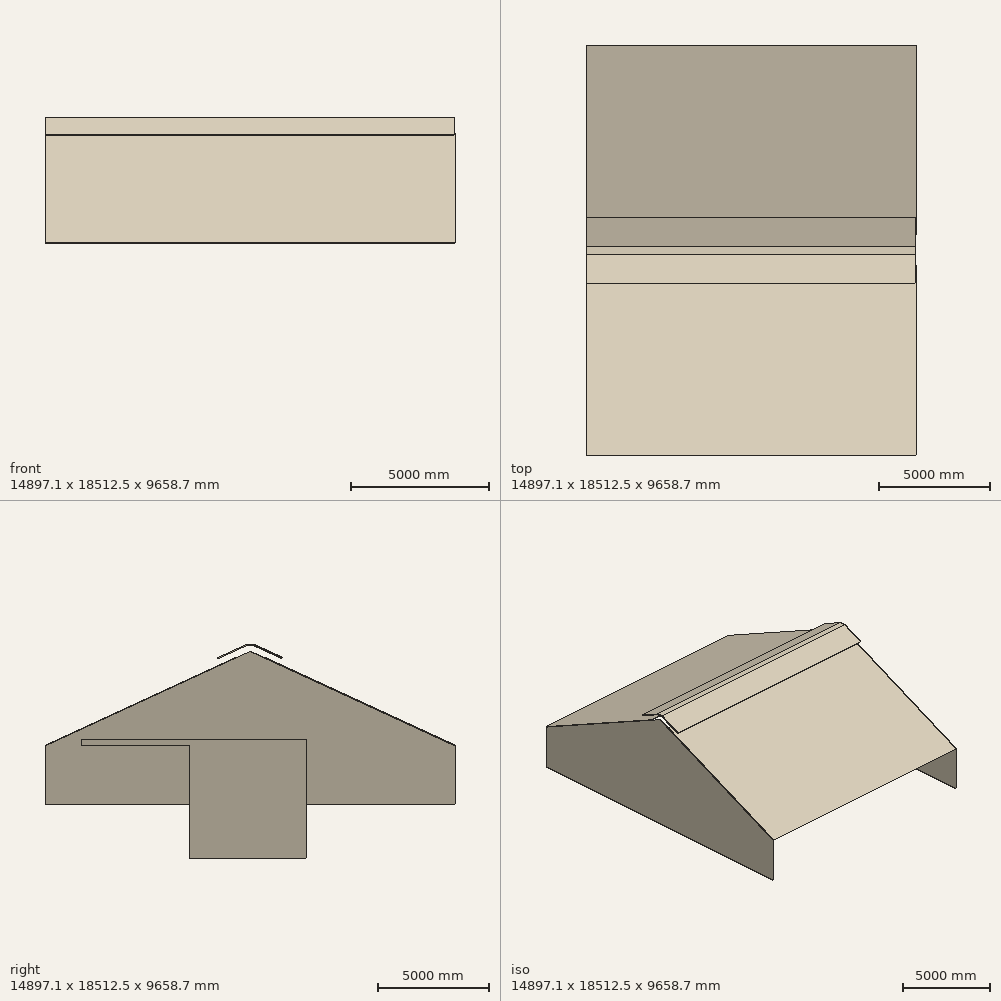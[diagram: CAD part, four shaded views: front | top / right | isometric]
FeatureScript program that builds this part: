
annotation { "Feature Type Name" : "Feature", "Feature Type Description" : "" }
export const myFeature = defineFeature(function(context is Context, id is Id, definition is map)
    precondition{}
    {
        {
            var Q0;
            Q0=qCreatedBy(makeId("Right.planeOp"),FACE);
            var sketch = newSketch(context, id + "F0", { "sketchPlane" : qUnion([Q0])});
            skLineSegment(sketch, "E0.bottom", {"start": v(-9245.6, 1320.8) * mm, "end": v(9245.6, 1320.8) * mm});
            skLineSegment(sketch, "E0.top", {"start": v(-9245.6, -1320.8) * mm, "end": v(9245.6, -1320.8) * mm});
            skLineSegment(sketch, "E0.left", {"start": v(-9245.6, 1320.8) * mm, "end": v(-9245.6, -1320.8) * mm});
            skLineSegment(sketch, "E0.right", {"start": v(9245.6, 1320.8) * mm, "end": v(9245.6, -1320.8) * mm});
            skPoint(sketch, "E0.middle", {"position": v(0, 0) * mm});
            skLineSegment(sketch, "E1", {"start": v(9245.6, 1320.8) * mm, "end": v(0, 5588) * mm});
            skLineSegment(sketch, "E2", {"start": v(0, 5588) * mm, "end": v(-9245.6, 1320.8) * mm});
            skSolve(sketch);
        }
        {
            var Q0;
            Q0=makeQuery(id+"F0.imprint","IMPRINT",FACE,{"disambiguationData":[TD([[makeQuery(id+"F0.imprint","IMPRINT",EDGE,{"derivedFrom":sQuery(id+"F0.wireOp",EDGE,"E0.bottom")}),1.0]])]});
            var Q1;
            Q1=makeQuery(id+"F0.imprint","IMPRINT",FACE,{"disambiguationData":[TD([[makeQuery(id+"F0.imprint","IMPRINT",EDGE,{"derivedFrom":sQuery(id+"F0.wireOp",EDGE,"E0.bottom")}),-1.0]])]});
            extrude(context, id + "F1", {"entities" : qUnion([Q0, Q1]), "depth" : 5.08 * mm, "offsetDistance" : 25.4 * mm});
        }
        {
            var Q0;
            Q0=makeQuery(id+"F1.opExtrude","CAP_FACE",FACE,{"disambiguationData":[OSD([sQuery(id+"F0.wireOp",EDGE,"E0.top"),sQuery(id+"F0.wireOp",EDGE,"E0.left"),sQuery(id+"F0.wireOp",EDGE,"E0.right"),sQuery(id+"F0.wireOp",EDGE,"E1"),sQuery(id+"F0.wireOp",EDGE,"E2")])],"isStart":false});
            var sketch = newSketch(context, id + "F2", { "sketchPlane" : qUnion([Q0])});
            skLineSegment(sketch, "E3.0", {"start": v(-9245.6, 1320.8) * mm, "end": v(-9245.6, -1320.8) * mm, "construction": true});
            skLineSegment(sketch, "E3.1", {"start": v(0, 5588) * mm, "end": v(-9245.6, 1320.8) * mm});
            skLineSegment(sketch, "E4.0", {"start": v(9245.6, 1320.8) * mm, "end": v(0, 5588) * mm});
            skLineSegment(sketch, "E5.0", {"start": v(9245.6, 1320.8) * mm, "end": v(9245.6, -1320.8) * mm, "construction": true});
            skLineSegment(sketch, "E6", {"start": v(-9245.6, 1320.8) * mm, "end": v(-9256.24, 1343.86) * mm});
            skLineSegment(sketch, "E7", {"start": v(-9256.24, 1343.86) * mm, "end": v(0, 5615.97) * mm});
            skLineSegment(sketch, "E8", {"start": v(0, 5615.97) * mm, "end": v(9256.24, 1343.86) * mm});
            skLineSegment(sketch, "E9", {"start": v(9245.6, 1320.8) * mm, "end": v(9256.24, 1343.86) * mm});
            skLineSegment(sketch, "E10", {"start": v(-671.04, 5306.26) * mm, "end": v(-660.4, 5283.2) * mm});
            skLineSegment(sketch, "E11", {"start": v(-660.4, 5283.2) * mm, "end": v(660.4, 5283.2) * mm, "construction": true});
            skLineSegment(sketch, "E12", {"start": v(660.4, 5283.2) * mm, "end": v(671.04, 5306.26) * mm});
            skSolve(sketch);
        }
        {
            var Q0;
            {var subQ0=sQuery(id+"F2.wireOp",EDGE,"E6");Q0=makeQuery(id+"F2.imprint","IMPRINT",FACE,{"disambiguationData":[TD([[makeQuery(id+"F2.imprint","IMPRINT",EDGE,{"derivedFrom":subQ0}),-1.0]])]});}
            var Q1;
            {var subQ0=sQuery(id+"F2.wireOp",EDGE,"E9");Q1=makeQuery(id+"F2.imprint","IMPRINT",FACE,{"disambiguationData":[TD([[makeQuery(id+"F2.imprint","IMPRINT",EDGE,{"derivedFrom":subQ0}),1.0]])]});}
            extrude(context, id + "F3", {"entities" : qUnion([Q0, Q1]), "depth" : 14874.24 * mm, "offsetDistance" : 25.4 * mm});
        }
        {
            var Q0;
            Q0=makeQuery(id+"F1.opExtrude","CAP_FACE",FACE,{"disambiguationData":[OSD([sQuery(id+"F0.wireOp",EDGE,"E0.top"),sQuery(id+"F0.wireOp",EDGE,"E0.left"),sQuery(id+"F0.wireOp",EDGE,"E0.right"),sQuery(id+"F0.wireOp",EDGE,"E1"),sQuery(id+"F0.wireOp",EDGE,"E2")])],"isStart":true});
            var sketch = newSketch(context, id + "F4", { "sketchPlane" : qUnion([Q0])});
            skLineSegment(sketch, "E13.0", {"start": v(-9245.6, 1320.8) * mm, "end": v(0, 5588) * mm, "construction": true});
            skLineSegment(sketch, "E13.1", {"start": v(0, 5588) * mm, "end": v(9245.6, 1320.8) * mm, "construction": true});
            skLineSegment(sketch, "E14", {"start": v(-1448.53, 5255.15) * mm, "end": v(-152.4, 5853.36) * mm});
            skLineSegment(sketch, "E15", {"start": v(-152.4, 5853.36) * mm, "end": v(152.4, 5853.36) * mm});
            skLineSegment(sketch, "E16", {"start": v(152.4, 5853.36) * mm, "end": v(1448.53, 5255.15) * mm});
            skLineSegment(sketch, "E17", {"start": v(-1448.53, 5255.15) * mm, "end": v(-1320.8, 4978.4) * mm, "construction": true});
            skLineSegment(sketch, "E18", {"start": v(-1320.8, 4978.4) * mm, "end": v(1320.8, 4978.4) * mm, "construction": true});
            skLineSegment(sketch, "E19", {"start": v(1320.8, 4978.4) * mm, "end": v(1448.53, 5255.15) * mm, "construction": true});
            skLineSegment(sketch, "E20", {"start": v(-1448.53, 5255.15) * mm, "end": v(-1469.82, 5301.27) * mm});
            skLineSegment(sketch, "E21", {"start": v(-1469.82, 5301.27) * mm, "end": v(-173.69, 5899.48) * mm});
            skLineSegment(sketch, "E22", {"start": v(-173.69, 5899.48) * mm, "end": v(173.69, 5899.48) * mm});
            skLineSegment(sketch, "E23", {"start": v(173.69, 5899.48) * mm, "end": v(1473.21, 5299.7) * mm});
            skLineSegment(sketch, "E24", {"start": v(1473.21, 5299.7) * mm, "end": v(1448.53, 5255.15) * mm});
            skLineSegment(sketch, "E25", {"start": v(-152.4, 5853.36) * mm, "end": v(-173.69, 5899.48) * mm, "construction": true});
            skLineSegment(sketch, "E26", {"start": v(152.4, 5853.36) * mm, "end": v(173.69, 5899.48) * mm, "construction": true});
            skSolve(sketch);
        }
        {
            var Q0;
            Q0=makeQuery(id+"F4.imprint","IMPRINT",FACE,{"disambiguationData":[TD([[makeQuery(id+"F4.imprint","IMPRINT",EDGE,{"derivedFrom":sQuery(id+"F4.wireOp",EDGE,"E14")}),1.0]])]});
            extrude(context, id + "F5", {"entities" : qUnion([Q0]), "oppositeDirection" : true, "depth" : 14874.24 * mm, "offsetDistance" : 25.4 * mm});
        }
        {
            var Q0;
            Q0=makeQuery(id+"F3.opExtrude","CAP_FACE",FACE,{"disambiguationData":[OSD([sQuery(id+"F2.wireOp",EDGE,"E3.1"),sQuery(id+"F2.wireOp",EDGE,"E6"),sQuery(id+"F2.wireOp",EDGE,"E7"),sQuery(id+"F2.wireOp",EDGE,"E10")])],"isStart":false});
            var sketch = newSketch(context, id + "F6", { "sketchPlane" : qUnion([Q0])});
            skLineSegment(sketch, "E27.0.0", {"start": v(-660.4, 5283.2) * mm, "end": v(-671.04, 5306.26) * mm, "construction": true});
            skLineSegment(sketch, "E27.0.1", {"start": v(-671.04, 5306.26) * mm, "end": v(-9256.24, 1343.86) * mm, "construction": true});
            skLineSegment(sketch, "E27.0.2", {"start": v(-9256.24, 1343.86) * mm, "end": v(-9245.6, 1320.8) * mm});
            skLineSegment(sketch, "E27.0.3", {"start": v(-9245.6, 1320.8) * mm, "end": v(-660.4, 5283.2) * mm});
            skLineSegment(sketch, "E28.0.0", {"start": v(660.4, 5283.2) * mm, "end": v(9245.6, 1320.8) * mm});
            skLineSegment(sketch, "E28.0.1", {"start": v(9245.6, 1320.8) * mm, "end": v(9256.24, 1343.86) * mm});
            skLineSegment(sketch, "E28.0.2", {"start": v(9256.24, 1343.86) * mm, "end": v(671.04, 5306.26) * mm, "construction": true});
            skLineSegment(sketch, "E28.0.3", {"start": v(671.04, 5306.26) * mm, "end": v(660.4, 5283.2) * mm});
            skPoint(sketch, "E29.0", {"position": v(-9245.6, -1320.8) * mm});
            skPoint(sketch, "E30.0", {"position": v(9245.6, -1320.8) * mm});
            skLineSegment(sketch, "E31", {"start": v(-9245.6, 1320.8) * mm, "end": v(-9245.6, -1320.8) * mm});
            skLineSegment(sketch, "E32", {"start": v(-2540, -1320.8) * mm, "end": v(-2540, 1117.6) * mm});
            skLineSegment(sketch, "E33", {"start": v(-2540, 1117.6) * mm, "end": v(2336.8, 1117.6) * mm});
            skLineSegment(sketch, "E34", {"start": v(2336.8, 1117.6) * mm, "end": v(2336.8, -1320.8) * mm});
            skLineSegment(sketch, "E35", {"start": v(2336.8, -1320.8) * mm, "end": v(9245.6, -1320.8) * mm});
            skLineSegment(sketch, "E36", {"start": v(9245.6, 1320.8) * mm, "end": v(9245.6, -1320.8) * mm});
            skPoint(sketch, "E37.0", {"position": v(0, 5588) * mm});
            skLineSegment(sketch, "E38", {"start": v(-660.4, 5283.2) * mm, "end": v(0, 5588) * mm});
            skLineSegment(sketch, "E39", {"start": v(660.4, 5283.2) * mm, "end": v(0, 5588) * mm});
            skLineSegment(sketch, "E40", {"start": v(-9245.6, -1320.8) * mm, "end": v(-2540, -1320.8) * mm});
            skSolve(sketch);
        }
        {
            var Q0;
            Q0=makeQuery(id+"F6.imprint","IMPRINT",FACE,{"disambiguationData":[TD([[makeQuery(id+"F6.imprint","IMPRINT",EDGE,{"derivedFrom":sQuery(id+"F6.wireOp",EDGE,"E27.0.3")}),1.0]])]});
            extrude(context, id + "F7", {"entities" : qUnion([Q0]), "depth" : 5.08 * mm, "offsetDistance" : 25.4 * mm});
        }
        {
            var Q0;
            Q0=makeQuery(id+"F7.opExtrude","CAP_FACE",FACE,{"disambiguationData":[OSD([sQuery(id+"F6.wireOp",EDGE,"E27.0.3"),sQuery(id+"F6.wireOp",EDGE,"E28.0.0"),sQuery(id+"F6.wireOp",EDGE,"E31"),sQuery(id+"F6.wireOp",EDGE,"E32"),sQuery(id+"F6.wireOp",EDGE,"E33"),sQuery(id+"F6.wireOp",EDGE,"E34"),sQuery(id+"F6.wireOp",EDGE,"E35"),sQuery(id+"F6.wireOp",EDGE,"E36"),sQuery(id+"F6.wireOp",EDGE,"E38"),sQuery(id+"F6.wireOp",EDGE,"E39"),sQuery(id+"F6.wireOp",EDGE,"E40")])],"isStart":false});
            var sketch = newSketch(context, id + "F8", { "sketchPlane" : qUnion([Q0])});
            skLineSegment(sketch, "E41.0", {"start": v(-2540, -1320.8) * mm, "end": v(-2540, 1117.6) * mm, "construction": true});
            skLineSegment(sketch, "E42.0", {"start": v(-2540, 1117.6) * mm, "end": v(2336.8, 1117.6) * mm, "construction": true});
            skLineSegment(sketch, "E43.0", {"start": v(2336.8, 1117.6) * mm, "end": v(2336.8, -1320.8) * mm, "construction": true});
            skLineSegment(sketch, "E44.top", {"start": v(2540, -3759.2) * mm, "end": v(-2743.2, -3759.2) * mm});
            skLineSegment(sketch, "E44.left", {"start": v(2540, 1320.8) * mm, "end": v(2540, -3759.2) * mm});
            skLineSegment(sketch, "E44.right", {"start": v(-2743.2, 1320.8) * mm, "end": v(-2743.2, -3759.2) * mm});
            skLineSegment(sketch, "E45.bottom", {"start": v(-2743.2, 1320.8) * mm, "end": v(-7620, 1320.8) * mm});
            skLineSegment(sketch, "E45.top", {"start": v(2540, 1625.6) * mm, "end": v(-7620, 1625.6) * mm});
            skLineSegment(sketch, "E45.left", {"start": v(2540, 1320.8) * mm, "end": v(2540, 1625.6) * mm});
            skLineSegment(sketch, "E45.right", {"start": v(-7620, 1320.8) * mm, "end": v(-7620, 1625.6) * mm});
            skSolve(sketch);
        }
        {
            var Q0;
            {var subQ6=sQuery(id+"F8.wireOp",EDGE,"E45.bottom");Q0=makeQuery(id+"F8.imprint","IMPRINT",FACE,{"disambiguationData":[TD([[makeQuery(id+"F8.imprint","IMPRINT",EDGE,{"derivedFrom":subQ6}),-1.0]])]});}
            var Q1;
            {var subQ1=sQuery(id+"F8.wireOp",EDGE,"E44.top");Q1=makeQuery(id+"F8.imprint","IMPRINT",FACE,{"disambiguationData":[TD([[makeQuery(id+"F8.imprint","IMPRINT",EDGE,{"derivedFrom":subQ1}),-1.0]])]});}
            extrude(context, id + "F9", {"entities" : qUnion([Q0, Q1]), "depth" : 12.7 * mm, "offsetDistance" : 25.4 * mm});
        }
    });
